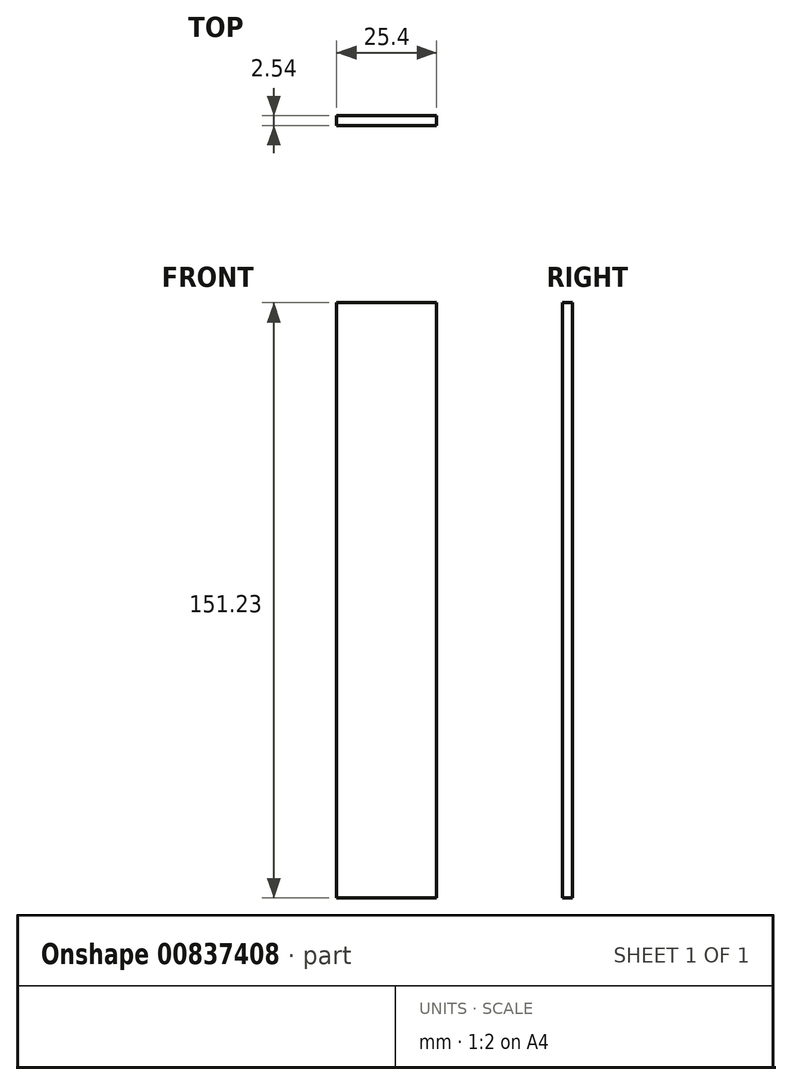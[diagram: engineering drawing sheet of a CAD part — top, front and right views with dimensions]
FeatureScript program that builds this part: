
annotation { "Feature Type Name" : "Feature", "Feature Type Description" : "" }
export const myFeature = defineFeature(function(context is Context, id is Id, definition is map)
    precondition{}
    {
        {
            var Q0;
            Q0=qCreatedBy(makeId("Front.planeOp"),FACE);
            var sketch = newSketch(context, id + "F0", { "sketchPlane" : qUnion([Q0])});
            skLineSegment(sketch, "E0", {"start": v(0, 0) * mm, "end": v(-12.7, 0) * mm});
            skLineSegment(sketch, "E1.MirrorCS", {"start": v(0, 0) * mm, "end": v(12.7, 0) * mm});
            skLineSegment(sketch, "E2", {"start": v(-12.7, 0) * mm, "end": v(-12.7, 100.03) * mm});
            skLineSegment(sketch, "E3", {"start": v(-12.7, 100.03) * mm, "end": v(12.7, 100.03) * mm});
            skLineSegment(sketch, "E4", {"start": v(12.7, 100.03) * mm, "end": v(12.7, 0) * mm});
            skLineSegment(sketch, "E5", {"start": v(-12.7, 100.03) * mm, "end": v(-12.7, 150.06) * mm});
            skLineSegment(sketch, "E6", {"start": v(-12.7, 150.06) * mm, "end": v(12.7, 150.06) * mm});
            skLineSegment(sketch, "E7", {"start": v(12.7, 150.06) * mm, "end": v(12.7, 100.03) * mm});
            skLineSegment(sketch, "E8", {"start": v(-12.7, 150.06) * mm, "end": v(-12.7, 151.23) * mm});
            skLineSegment(sketch, "E9", {"start": v(-12.7, 151.23) * mm, "end": v(12.7, 151.23) * mm});
            skLineSegment(sketch, "E10", {"start": v(12.7, 151.23) * mm, "end": v(12.7, 150.06) * mm});
            skSolve(sketch);
        }
        {
            var Q0;
            Q0=makeQuery(id+"F0.imprint","IMPRINT",FACE,{"disambiguationData":[TD([[makeQuery(id+"F0.imprint","IMPRINT",EDGE,{"derivedFrom":sQuery(id+"F0.wireOp",EDGE,"E0")}),-1.0]])]});
            var Q1;
            Q1=makeQuery(id+"F0.imprint","IMPRINT",FACE,{"disambiguationData":[TD([[makeQuery(id+"F0.imprint","IMPRINT",EDGE,{"derivedFrom":sQuery(id+"F0.wireOp",EDGE,"E3")}),1.0]])]});
            var Q2;
            Q2=makeQuery(id+"F0.imprint","IMPRINT",FACE,{"disambiguationData":[TD([[makeQuery(id+"F0.imprint","IMPRINT",EDGE,{"derivedFrom":sQuery(id+"F0.wireOp",EDGE,"E6")}),1.0]])]});
            extrude(context, id + "F1", {"entities" : qUnion([Q0, Q1, Q2]), "oppositeDirection" : true, "depth" : 2.54 * mm, "offsetDistance" : 25.4 * mm});
        }
    });
